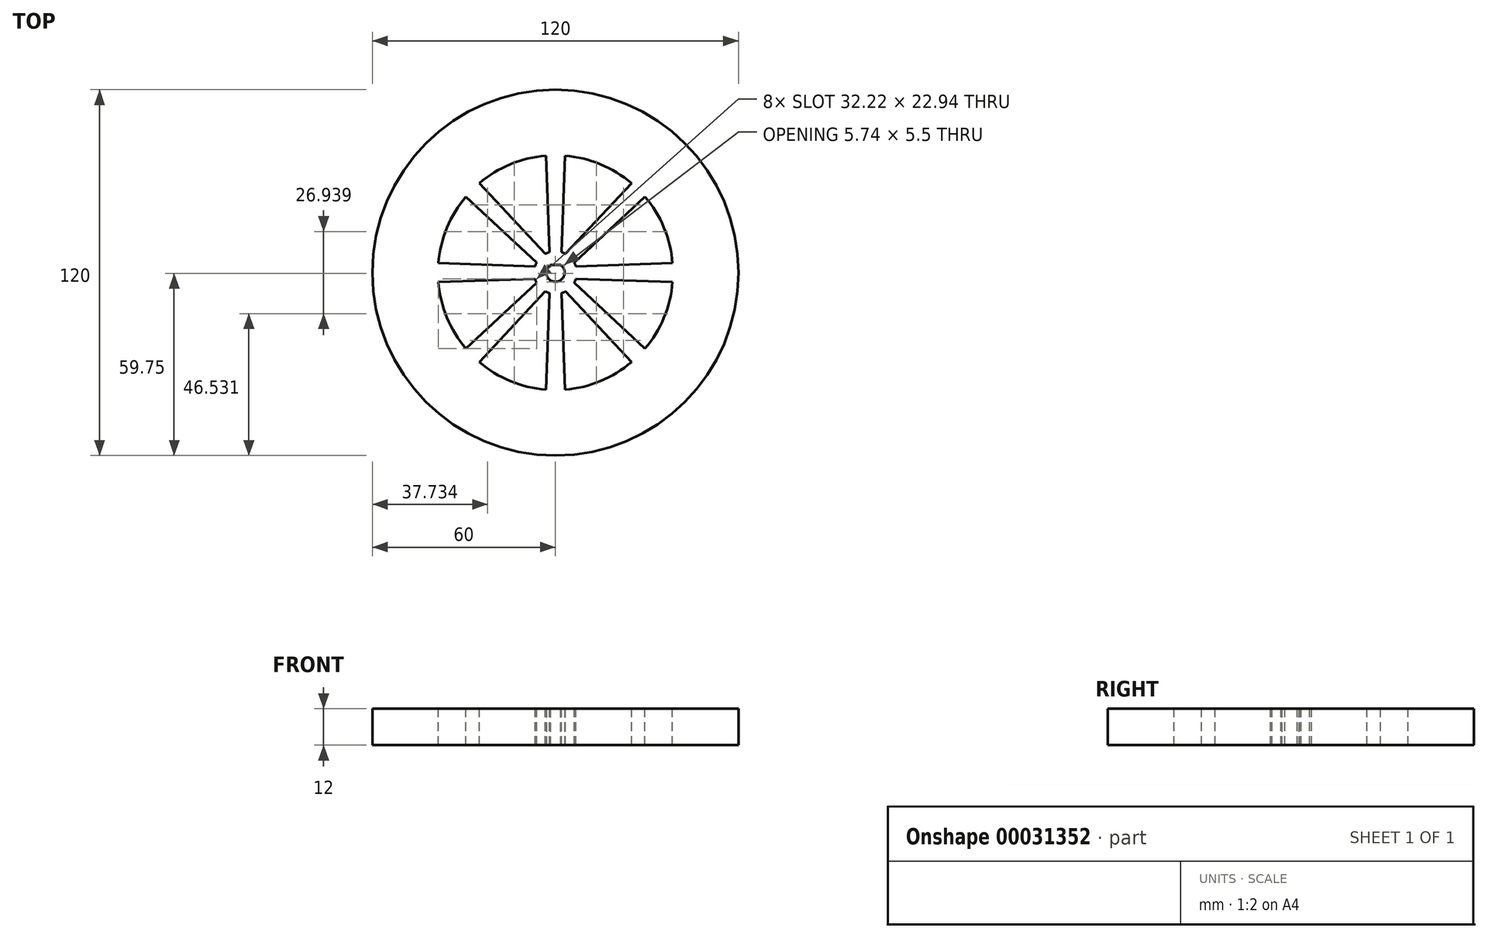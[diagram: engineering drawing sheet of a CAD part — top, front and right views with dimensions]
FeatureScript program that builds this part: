
annotation { "Feature Type Name" : "Feature", "Feature Type Description" : "" }
export const myFeature = defineFeature(function(context is Context, id is Id, definition is map)
    precondition{}
    {
        {
            var Q0;
            Q0=qCreatedBy(makeId("Top.planeOp"),FACE);
            var sketch = newSketch(context, id + "F0", { "sketchPlane" : qUnion([Q0])});
            skCircle(sketch, "E0", {"center": v(0, 0) * mm, "radius": 60 * mm});
            skArc(sketch, "E1", {"start": v(-1.66, 2.5) * mm, "mid": v(0, -3) * mm, "end": v(1.66, 2.5) * mm});
            skLineSegment(sketch, "E2", {"start": v(-1.66, 2.5) * mm, "end": v(1.66, 2.5) * mm});
            skSolve(sketch);
        }
        {
            var Q0;
            Q0 = qSketchRegion(id + "F0", true);
            extrude(context, id + "F1", {"entities" : qUnion([Q0]), "depth" : 12 * mm});
        }
        {
            var Q0;
            Q0=makeQuery(id+"F1.opExtrude","CAP_FACE",FACE,{"disambiguationData":[OSD([sQuery(id+"F0.wireOp",EDGE,"E0"),sQuery(id+"F0.wireOp",EDGE,"E1"),sQuery(id+"F0.wireOp",EDGE,"E2")])],"isStart":false});
            var sketch = newSketch(context, id + "F2", { "sketchPlane" : qUnion([Q0])});
            skArc(sketch, "E3", {"start": v(-2, 6.7) * mm, "mid": v(-2.68, 6.47) * mm, "end": v(-3.33, 6.16) * mm});
            skArc(sketch, "E4", {"start": v(-3.1, 38.37) * mm, "mid": v(-14.73, 35.57) * mm, "end": v(-24.94, 29.33) * mm});
            skLineSegment(sketch, "E5", {"start": v(0, 38.5) * mm, "end": v(0, 7) * mm, "construction": true});
            skLineSegment(sketch, "E6", {"start": v(-2, 6.7) * mm, "end": v(-3.1, 38.37) * mm});
            skLineSegment(sketch, "E7", {"start": v(2, 6.7) * mm, "end": v(3.1, 38.37) * mm});
            skLineSegment(sketch, "E8.1.0", {"start": v(27.22, 27.22) * mm, "end": v(4.95, 4.95) * mm, "construction": true});
            skLineSegment(sketch, "E8.1.1", {"start": v(6.16, 3.33) * mm, "end": v(29.33, 24.94) * mm});
            skLineSegment(sketch, "E8.1.2", {"start": v(3.33, 6.16) * mm, "end": v(24.94, 29.33) * mm});
            skLineSegment(sketch, "E8.2.0", {"start": v(38.5, 0) * mm, "end": v(7, 0) * mm, "construction": true});
            skLineSegment(sketch, "E8.2.1", {"start": v(6.7, -2) * mm, "end": v(38.37, -3.1) * mm});
            skLineSegment(sketch, "E8.2.2", {"start": v(6.7, 2) * mm, "end": v(38.37, 3.1) * mm});
            skLineSegment(sketch, "E8.3.0", {"start": v(27.22, -27.22) * mm, "end": v(4.95, -4.95) * mm, "construction": true});
            skLineSegment(sketch, "E8.3.1", {"start": v(3.33, -6.16) * mm, "end": v(24.94, -29.33) * mm});
            skLineSegment(sketch, "E8.3.2", {"start": v(6.16, -3.33) * mm, "end": v(29.33, -24.94) * mm});
            skLineSegment(sketch, "E8.anchor1", {"start": v(0, 0) * mm, "end": v(0, 7) * mm, "construction": true});
            skLineSegment(sketch, "E8.anchor2", {"start": v(0, 0) * mm, "end": v(-4.95, 4.95) * mm, "construction": true});
            skArc(sketch, "E9.trimOffspring", {"start": v(3.33, 6.16) * mm, "mid": v(2.68, 6.47) * mm, "end": v(2, 6.7) * mm});
            skArc(sketch, "E10.trimOffspring", {"start": v(6.7, 2) * mm, "mid": v(6.47, 2.68) * mm, "end": v(6.16, 3.33) * mm});
            skArc(sketch, "E11.trimOffspring", {"start": v(-6.16, 3.33) * mm, "mid": v(-6.47, 2.68) * mm, "end": v(-6.7, 2) * mm});
            skArc(sketch, "E12.trimOffspring", {"start": v(24.94, 29.33) * mm, "mid": v(14.73, 35.57) * mm, "end": v(3.1, 38.37) * mm});
            skArc(sketch, "E13.trimOffspring", {"start": v(38.37, 3.1) * mm, "mid": v(35.57, 14.73) * mm, "end": v(29.33, 24.94) * mm});
            skArc(sketch, "E14.trimOffspring", {"start": v(-29.33, 24.94) * mm, "mid": v(-35.57, 14.73) * mm, "end": v(-38.37, 3.1) * mm});
            skLineSegment(sketch, "E15.2.4.0", {"start": v(0, -38.5) * mm, "end": v(0, -7) * mm, "construction": true});
            skLineSegment(sketch, "E15.3.4.0", {"start": v(-2, -6.7) * mm, "end": v(-3.1, -38.37) * mm});
            skLineSegment(sketch, "E15.6.4.0", {"start": v(2, -6.7) * mm, "end": v(3.1, -38.37) * mm});
            skLineSegment(sketch, "E15.2.5.0", {"start": v(-27.22, -27.22) * mm, "end": v(-4.95, -4.95) * mm, "construction": true});
            skLineSegment(sketch, "E15.3.5.0", {"start": v(-6.16, -3.33) * mm, "end": v(-29.33, -24.94) * mm});
            skLineSegment(sketch, "E15.6.5.0", {"start": v(-3.33, -6.16) * mm, "end": v(-24.94, -29.33) * mm});
            skLineSegment(sketch, "E15.2.6.0", {"start": v(-38.5, 0) * mm, "end": v(-7, 0) * mm, "construction": true});
            skLineSegment(sketch, "E15.3.6.0", {"start": v(-6.7, 2) * mm, "end": v(-38.37, 3.1) * mm});
            skLineSegment(sketch, "E15.6.6.0", {"start": v(-6.7, -2) * mm, "end": v(-38.37, -3.1) * mm});
            skLineSegment(sketch, "E16.2.7.0", {"start": v(-27.22, 27.22) * mm, "end": v(-4.95, 4.95) * mm, "construction": true});
            skLineSegment(sketch, "E16.3.7.0", {"start": v(-3.33, 6.16) * mm, "end": v(-24.94, 29.33) * mm});
            skLineSegment(sketch, "E16.6.7.0", {"start": v(-6.16, 3.33) * mm, "end": v(-29.33, 24.94) * mm});
            skArc(sketch, "E17.trimOffspring", {"start": v(-38.37, -3.1) * mm, "mid": v(-35.57, -14.73) * mm, "end": v(-29.33, -24.94) * mm});
            skArc(sketch, "E18.trimOffspring", {"start": v(29.33, -24.94) * mm, "mid": v(35.57, -14.73) * mm, "end": v(38.37, -3.1) * mm});
            skArc(sketch, "E19.trimOffspring", {"start": v(3.1, -38.37) * mm, "mid": v(14.73, -35.57) * mm, "end": v(24.94, -29.33) * mm});
            skArc(sketch, "E20.trimOffspring", {"start": v(-24.94, -29.33) * mm, "mid": v(-14.73, -35.57) * mm, "end": v(-3.1, -38.37) * mm});
            skArc(sketch, "E21.trimOffspring", {"start": v(-6.7, -2) * mm, "mid": v(-6.47, -2.68) * mm, "end": v(-6.16, -3.33) * mm});
            skArc(sketch, "E22.trimOffspring", {"start": v(-3.33, -6.16) * mm, "mid": v(-2.68, -6.47) * mm, "end": v(-2, -6.7) * mm});
            skArc(sketch, "E23.trimOffspring", {"start": v(2, -6.7) * mm, "mid": v(2.68, -6.47) * mm, "end": v(3.33, -6.16) * mm});
            skArc(sketch, "E24.trimOffspring", {"start": v(6.16, -3.33) * mm, "mid": v(6.47, -2.68) * mm, "end": v(6.7, -2) * mm});
            skSolve(sketch);
        }
        {
            var Q0;
            Q0 = qSketchRegion(id + "F2", true);
            extrude(context, id + "F3", {"entities" : qUnion([Q0]), "operationType" : NewBodyOperationType.REMOVE, "oppositeDirection" : true, "depth" : 25 * mm});
        }
    });
